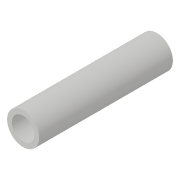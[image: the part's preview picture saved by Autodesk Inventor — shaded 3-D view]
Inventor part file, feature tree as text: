
AUTODESK INVENTOR PART (.ipt)
format: ipt  version: 2018 (Build 220112000, 112)  size: 77,824 bytes
history: native  units: in
note: dims shown in document units (in); Inventor stores cm internally (conversion verified against a paired STEP export)
features: extrude x1, sketch x1
ambient origin geometry x8: Origin, YZ Plane, XZ Plane, XY Plane, X Axis, Y Axis, Z Axis, Center Point
bodies: Solid1 (feature_tree)
feature tree (2):
  extrude  "Extrusion1"  Depth=0.9843in
  sketch  "Sketch1"  dims[d0=0.1654in d1=0.2362in d2=0.9843in d3=0.0in]
